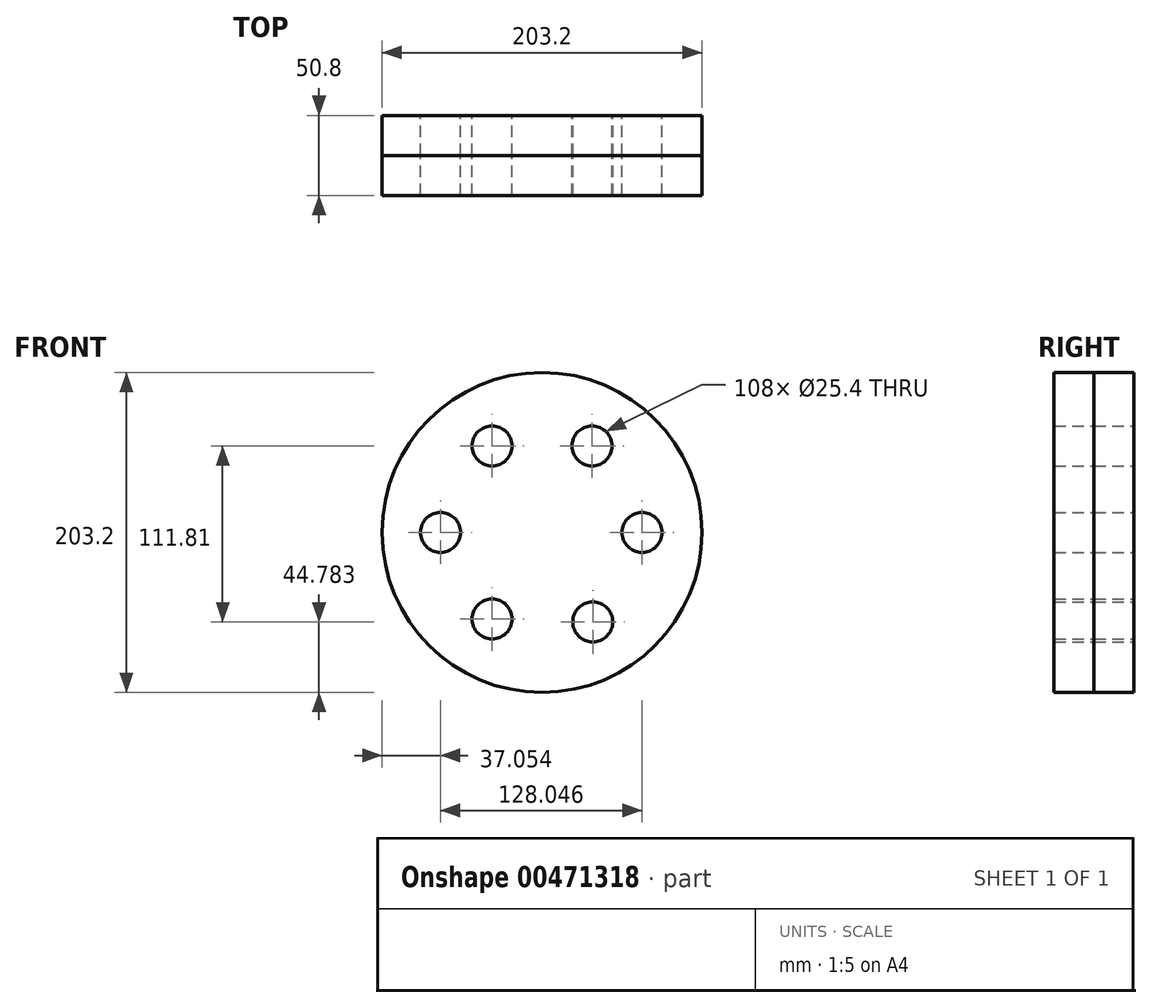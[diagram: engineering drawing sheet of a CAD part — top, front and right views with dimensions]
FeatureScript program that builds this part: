
annotation { "Feature Type Name" : "Feature", "Feature Type Description" : "" }
export const myFeature = defineFeature(function(context is Context, id is Id, definition is map)
    precondition{}
    {
        {
            var Q0;
            Q0=qCreatedBy(makeId("Front.planeOp"),FACE);
            var sketch = newSketch(context, id + "F0", { "sketchPlane" : qUnion([Q0])});
            skCircle(sketch, "E0", {"center": v(0, 0) * mm, "radius": 101.6 * mm});
            skCircle(sketch, "E1.cCircle", {"center": v(0, 0) * mm, "radius": 55 * mm, "construction": true});
            skLineSegment(sketch, "E1.0", {"start": v(31.75, -55) * mm, "end": v(-31.75, -55) * mm});
            skLineSegment(sketch, "E1.1", {"start": v(-31.75, -55) * mm, "end": v(-63.5, 0) * mm});
            skLineSegment(sketch, "E1.2", {"start": v(-63.5, 0) * mm, "end": v(-31.75, 55) * mm});
            skLineSegment(sketch, "E1.3", {"start": v(-31.75, 55) * mm, "end": v(31.75, 55) * mm});
            skLineSegment(sketch, "E1.4", {"start": v(31.75, 55) * mm, "end": v(63.5, 0) * mm});
            skLineSegment(sketch, "E1.5", {"start": v(63.5, 0) * mm, "end": v(31.75, -55) * mm});
            skPoint(sketch, "E1.0.midPoint", {"position": v(0, -55) * mm});
            skCircle(sketch, "E2", {"center": v(-31.75, 55) * mm, "radius": 12.7 * mm});
            skCircle(sketch, "E3", {"center": v(31.75, 55) * mm, "radius": 12.7 * mm});
            skCircle(sketch, "E4", {"center": v(63.5, 0) * mm, "radius": 12.7 * mm});
            skCircle(sketch, "E5", {"center": v(32.2, -56.82) * mm, "radius": 12.7 * mm});
            skCircle(sketch, "E6", {"center": v(-31.75, -55) * mm, "radius": 12.7 * mm});
            skCircle(sketch, "E7", {"center": v(-64.55, 0.06) * mm, "radius": 12.7 * mm});
            skSolve(sketch);
        }
        {
            var Q0;
            Q0 = qSketchRegion(id + "F0", true);
            var Q1;
            {var subQ13=sQuery(id+"F0.wireOp",EDGE,"E5");var subQ15=sQuery(id+"F0.wireOp",EDGE,"E1.0");var subQ16=makeQuery(id+"F0.imprint","INTERSECT",VERTEX,{"derivedFrom":[subQ15,subQ13]});Q1=makeQuery(id+"F0.imprint","IMPRINT",FACE,{"disambiguationData":[TD([[makeQuery(id+"F0.imprint","IMPRINT",EDGE,{"disambiguationData":[TD([[subQ16,-1.0]])],"derivedFrom":subQ15}),-1.0]])]});}
            extrude(context, id + "F1", {"entities" : qUnion([Q0, Q1]), "depth" : 25.4 * mm});
        }
        {
            var Q0;
            Q0=makeQuery(id+"F1.opExtrude","CAP_FACE",FACE,{"disambiguationData":[OSD([sQuery(id+"F0.wireOp",EDGE,"E0"),sQuery(id+"F0.wireOp",EDGE,"E2"),sQuery(id+"F0.wireOp",EDGE,"E3"),sQuery(id+"F0.wireOp",EDGE,"E4"),sQuery(id+"F0.wireOp",EDGE,"E5"),sQuery(id+"F0.wireOp",EDGE,"E6"),sQuery(id+"F0.wireOp",EDGE,"E7")])],"isStart":false});
            var sketch = newSketch(context, id + "F2", { "sketchPlane" : qUnion([Q0])});
            skCircle(sketch, "E8.0", {"center": v(-31.75, 55) * mm, "radius": 12.7 * mm});
            skCircle(sketch, "E9.0", {"center": v(63.5, 0) * mm, "radius": 12.7 * mm});
            skCircle(sketch, "E10.0", {"center": v(-31.75, -55) * mm, "radius": 12.7 * mm});
            skCircle(sketch, "E11.0", {"center": v(-64.55, 0.06) * mm, "radius": 12.7 * mm});
            skCircle(sketch, "E12.0", {"center": v(0, 0) * mm, "radius": 101.6 * mm});
            skCircle(sketch, "E13.0", {"center": v(32.2, -56.82) * mm, "radius": 12.7 * mm});
            skCircle(sketch, "E14.0", {"center": v(31.75, 55) * mm, "radius": 12.7 * mm});
            skSolve(sketch);
        }
        {
            var Q0;
            Q0 = qSketchRegion(id + "F2", true);
            extrude(context, id + "F3", {"entities" : qUnion([Q0]), "depth" : 25.4 * mm});
        }
    });
